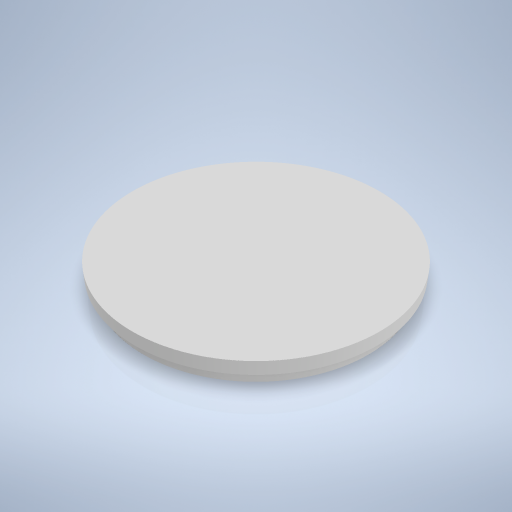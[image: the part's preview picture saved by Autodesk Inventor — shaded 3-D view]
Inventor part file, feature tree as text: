
AUTODESK INVENTOR PART (.ipt)
format: ipt  version: 2024.2 (Build 282272000, 272)  size: 224,768 bytes
history: native  units: mm
features: revolve x1, sketch x1
ambient origin geometry x8: Origin, YZ Plane, XZ Plane, XY Plane, X Axis, Y Axis, Z Axis, Center Point
bodies: Volumenkörper1 (feature_tree)
feature tree (2):
  revolve  "Umdrehung1"
  sketch  "Skizze1"  dims[d0=3.0mm d1=3.0mm d2=63.0mm d3=66.0mm d4=90.0deg]
